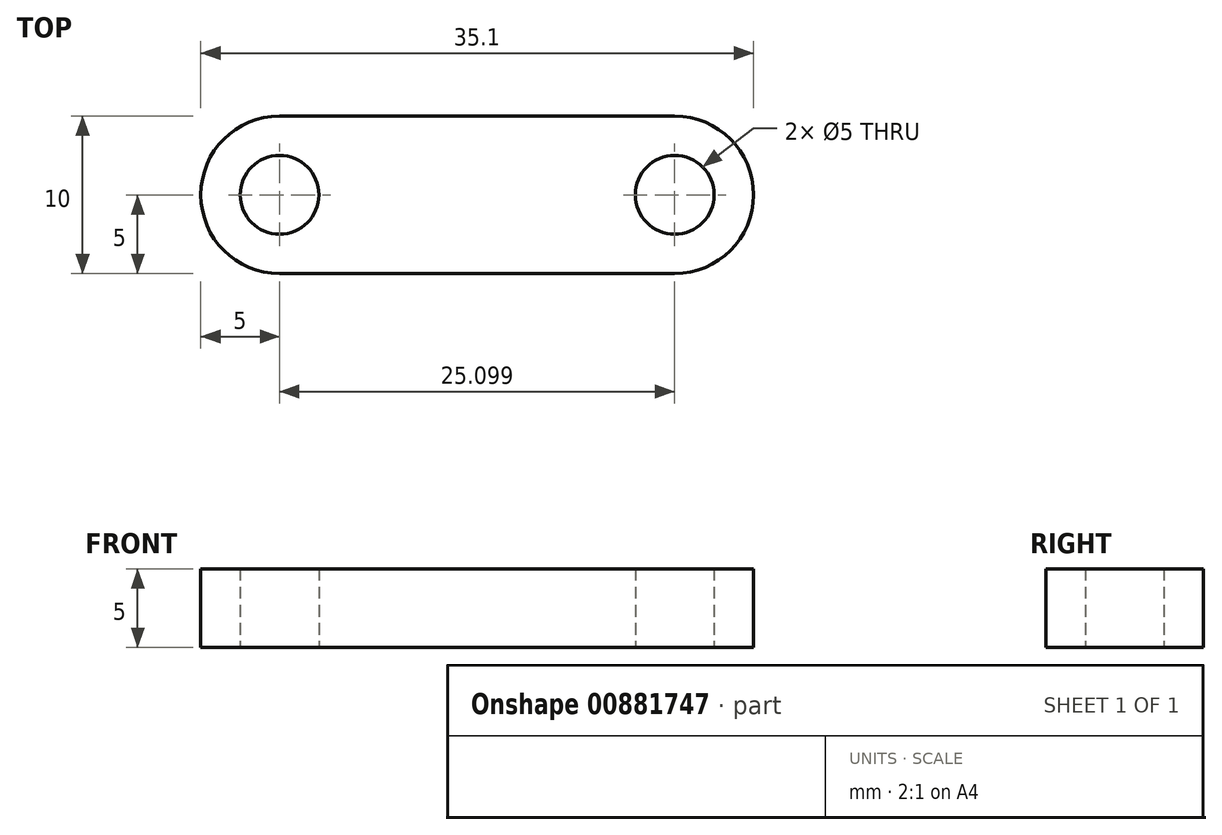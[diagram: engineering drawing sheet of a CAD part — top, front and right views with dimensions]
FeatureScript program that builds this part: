
annotation { "Feature Type Name" : "Feature", "Feature Type Description" : "" }
export const myFeature = defineFeature(function(context is Context, id is Id, definition is map)
    precondition{}
    {
        {
            var Q0;
            Q0=qCreatedBy(makeId("Top.planeOp"),FACE);
            var sketch = newSketch(context, id + "F0", { "sketchPlane" : qUnion([Q0])});
            skCircle(sketch, "E0", {"center": v(0, 0) * mm, "radius": 5 * mm});
            skCircle(sketch, "E1", {"center": v(25.1, 0) * mm, "radius": 5 * mm});
            skCircle(sketch, "E2", {"center": v(0, 0) * mm, "radius": 2.5 * mm});
            skCircle(sketch, "E3", {"center": v(25.1, 0) * mm, "radius": 2.5 * mm});
            skLineSegment(sketch, "E4.bottom", {"start": v(0, -5) * mm, "end": v(25.1, -5) * mm});
            skLineSegment(sketch, "E4.top", {"start": v(0, 5) * mm, "end": v(25.1, 5) * mm});
            skLineSegment(sketch, "E4.left", {"start": v(0, -5) * mm, "end": v(0, 5) * mm});
            skLineSegment(sketch, "E4.right", {"start": v(25.1, -5) * mm, "end": v(25.1, 5) * mm});
            skSolve(sketch);
        }
        {
            var Q0;
            {var subQ0=sQuery(id+"F0.wireOp",EDGE,"E4.left");var subQ4=sQuery(id+"F0.wireOp",EDGE,"E2");var subQ5=makeQuery(id+"F0.imprint","INTERSECT",VERTEX,{"disambiguationData":[OD(0.0)],"derivedFrom":[subQ4,subQ0]});Q0=makeQuery(id+"F0.imprint","IMPRINT",FACE,{"disambiguationData":[TD([[makeQuery(id+"F0.imprint","IMPRINT",EDGE,{"disambiguationData":[TD([[subQ5,1.0]])],"derivedFrom":subQ4}),-1.0]])]});}
            var Q1;
            {var subQ0=sQuery(id+"F0.wireOp",EDGE,"E4.left");var subQ4=sQuery(id+"F0.wireOp",EDGE,"E2");var subQ5=makeQuery(id+"F0.imprint","INTERSECT",VERTEX,{"disambiguationData":[OD(0.0)],"derivedFrom":[subQ4,subQ0]});Q1=makeQuery(id+"F0.imprint","IMPRINT",FACE,{"disambiguationData":[TD([[makeQuery(id+"F0.imprint","IMPRINT",EDGE,{"disambiguationData":[TD([[subQ5,-1.0]])],"derivedFrom":subQ4}),-1.0]])]});}
            var Q2;
            {var subQ1=sQuery(id+"F0.wireOp",EDGE,"E4.bottom");Q2=makeQuery(id+"F0.imprint","IMPRINT",FACE,{"disambiguationData":[TD([[makeQuery(id+"F0.imprint","IMPRINT",EDGE,{"derivedFrom":subQ1}),1.0]])]});}
            var Q3;
            {var subQ0=sQuery(id+"F0.wireOp",EDGE,"E4.right");var subQ4=sQuery(id+"F0.wireOp",EDGE,"E3");var subQ5=makeQuery(id+"F0.imprint","INTERSECT",VERTEX,{"disambiguationData":[OD(0.0)],"derivedFrom":[subQ4,subQ0]});Q3=makeQuery(id+"F0.imprint","IMPRINT",FACE,{"disambiguationData":[TD([[makeQuery(id+"F0.imprint","IMPRINT",EDGE,{"disambiguationData":[TD([[subQ5,1.0]])],"derivedFrom":subQ4}),-1.0]])]});}
            var Q4;
            {var subQ0=sQuery(id+"F0.wireOp",EDGE,"E4.right");var subQ4=sQuery(id+"F0.wireOp",EDGE,"E3");var subQ5=makeQuery(id+"F0.imprint","INTERSECT",VERTEX,{"disambiguationData":[OD(0.0)],"derivedFrom":[subQ4,subQ0]});Q4=makeQuery(id+"F0.imprint","IMPRINT",FACE,{"disambiguationData":[TD([[makeQuery(id+"F0.imprint","IMPRINT",EDGE,{"disambiguationData":[TD([[subQ5,-1.0]])],"derivedFrom":subQ4}),-1.0]])]});}
            extrude(context, id + "F1", {"entities" : qUnion([Q0, Q1, Q2, Q3, Q4]), "depth" : 5 * mm, "offsetDistance" : 25 * mm});
        }
    });
